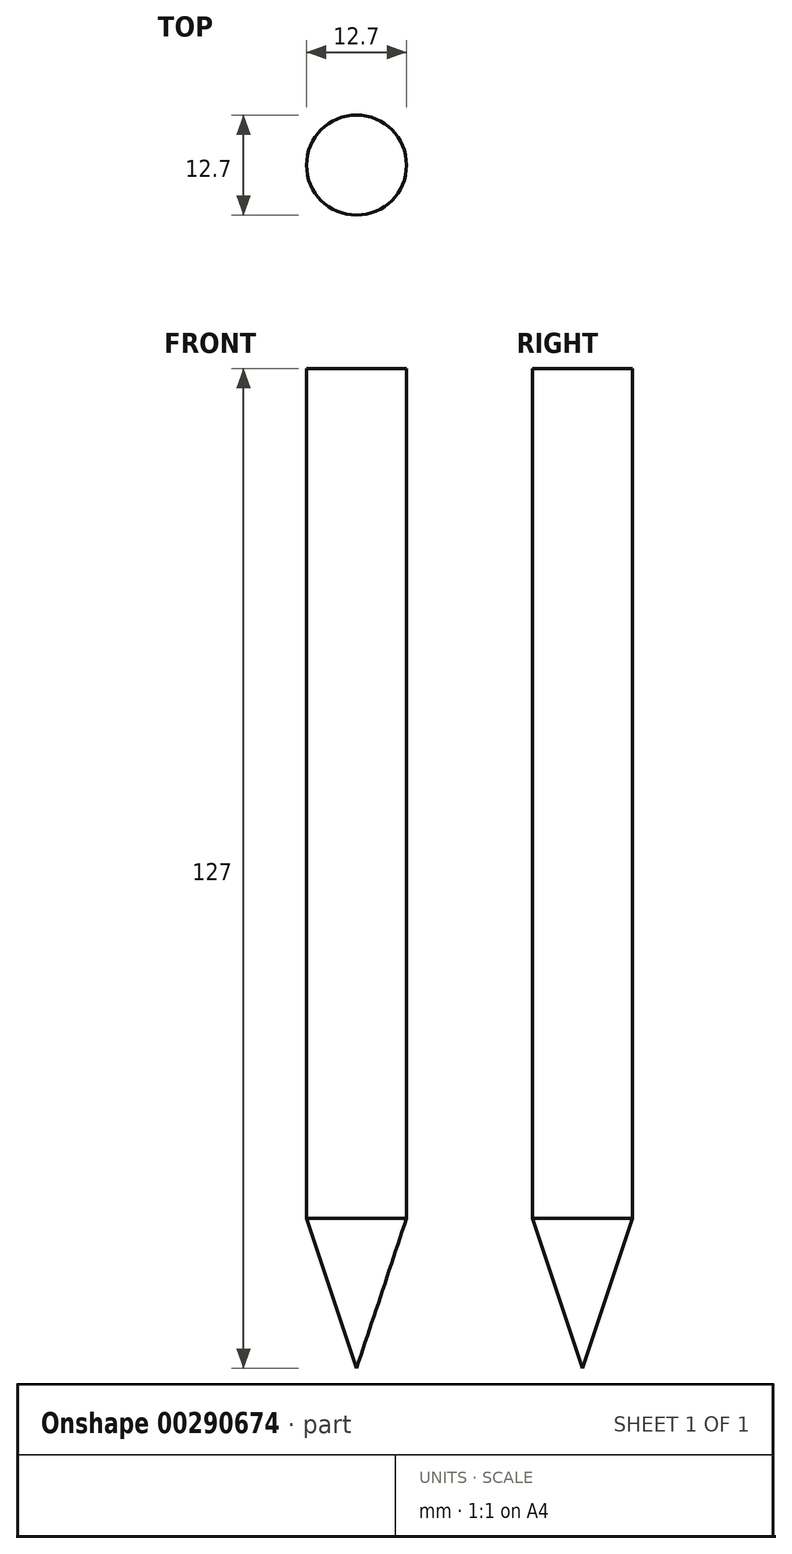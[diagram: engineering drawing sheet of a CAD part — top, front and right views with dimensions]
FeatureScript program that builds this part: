
annotation { "Feature Type Name" : "Feature", "Feature Type Description" : "" }
export const myFeature = defineFeature(function(context is Context, id is Id, definition is map)
    precondition{}
    {
        {
            var Q0;
            Q0=qCreatedBy(makeId("Top.planeOp"),FACE);
            var sketch = newSketch(context, id + "F0", { "sketchPlane" : qUnion([Q0])});
            skCircle(sketch, "E0", {"center": v(0, 0) * mm, "radius": 6.35 * mm});
            skSolve(sketch);
        }
        {
            var Q0;
            Q0=makeQuery(id+"F0.imprint","IMPRINT",FACE,{"disambiguationData":[TD([[makeQuery(id+"F0.imprint","IMPRINT",EDGE,{"derivedFrom":sQuery(id+"F0.wireOp",EDGE,"E0")}),1.0]])]});
            extrude(context, id + "F1", {"entities" : qUnion([Q0]), "depth" : 127 * mm});
        }
        {
            var Q0;
            Q0=makeQuery(id+"F1.opExtrude","CAP_EDGE",EDGE,{"disambiguationData":[OSD([sQuery(id+"F0.wireOp",EDGE,"E0")])],"isStart":true});
            chamfer(context, id + "F2", {"entities" : qUnion([Q0]), "chamferType" : ChamferType.TWO_OFFSETS, "width1" : 19.05 * mm, "oppositeDirection" : false, "width2" : 6.35 * mm, "tangentPropagation" : true});
        }
    });
